# Revit family: SeatingInc-Square_Table
name_source: partatom
category: Furniture
revit_build: Autodesk Revit MEP 2014 (Build: 20130308_1515(x64)
units: mm (PartAtom-declared; Revit-internal decimal feet)

## types (10) — shared parameters
Assembly Code = E2020200
Edge Band = STI - Black
Glide = STI - Black
Keynote = 12500
Leg = STI - Metal
Manufacturer = seating inc.
Table Top = STI - Maple
Type Comments = Table Square
URL = http://www.seatinginc.com

## per-type parameters (varying)
| type | Depth | Description | Height | Model | Width |
| Square-Table MS18R | 18" | Square Table 18"W 18"D 16"H | 16" | MS18R | 18" |
| Square-Table MS24R | 24" | Square Table 24"W 24"D 16"H | 16" | MS24R | 24" |
| Square-Table MS30R | 30" | Square Table 30"W 30"D 16"H | 16" | MS30R | 30" |
| Square-Table MS36R | 36" | Square Table 36"W 36"D 16"H | 16" | MS36R | 36" |
| Square-Table MS42R | 42" | Square Table 42"W 42"D 16"H | 16" | MS42R | 42" |
| Square-Table Tall MT18R | 18" | Square-Table Tall 18"W 18"D 21"H | 21" | MT18R | 18" |
| Square-Table Tall MT24R | 24" | Square-Table Tall 24"W 24"D 21"H | 21" | MT24R | 24" |
| Square-Table Tall MT30R | 30" | Square-Table Tall 30"W 30"D 21"H | 21" | MT30R | 30" |
| Square-Table Tall MT36R | 36" | Square-Table Tall 36"W 36"D 21"H | 21" | MT36R | 36" |
| Square-Table Tall MT42R | 42" | Square-Table Tall 42"W 42"D 21"H | 21" | MT42R | 42" |

## geometry (parser evidence)
native form markers: Sweep x1
no freeform markers — native parametric forms only
